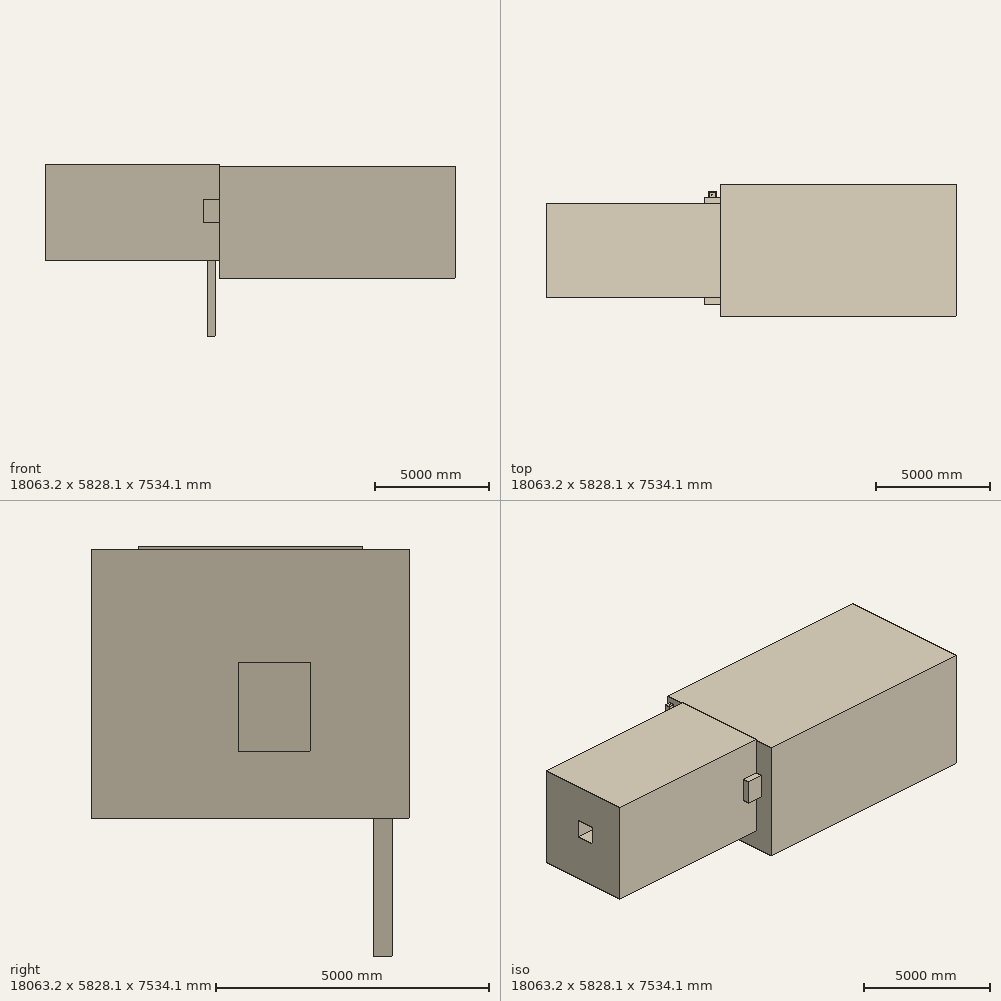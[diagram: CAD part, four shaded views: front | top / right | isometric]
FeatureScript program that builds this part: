
annotation { "Feature Type Name" : "Feature", "Feature Type Description" : "" }
export const myFeature = defineFeature(function(context is Context, id is Id, definition is map)
    precondition{}
    {
        {
            var Q0;
            Q0=qCreatedBy(makeId("Top.planeOp"),FACE);
            var sketch = newSketch(context, id + "F0", { "sketchPlane" : qUnion([Q0])});
            skLineSegment(sketch, "E0.bottom", {"start": v(-98.51, -97.6) * mm, "end": v(99.32, -97.6) * mm});
            skLineSegment(sketch, "E0.top", {"start": v(-98.51, 98.05) * mm, "end": v(99.32, 98.05) * mm});
            skLineSegment(sketch, "E0.left", {"start": v(-98.51, -97.6) * mm, "end": v(-98.51, 98.05) * mm});
            skLineSegment(sketch, "E0.right", {"start": v(99.32, -97.6) * mm, "end": v(99.32, 98.05) * mm});
            skSolve(sketch);
        }
        {
            var Q0;
            Q0 = qSketchRegion(id + "F0", true);
            extrude(context, id + "F1", {"entities" : qUnion([Q0]), "depth" : 1013.86 * mm, "offsetDistance" : 25.4 * mm});
        }
        {
            var Q0;
            Q0=makeQuery(id+"F1.opExtrude","CAP_FACE",FACE,{"disambiguationData":[OSD([sQuery(id+"F0.wireOp",EDGE,"E0.bottom"),sQuery(id+"F0.wireOp",EDGE,"E0.top"),sQuery(id+"F0.wireOp",EDGE,"E0.left"),sQuery(id+"F0.wireOp",EDGE,"E0.right")])],"isStart":false});
            var sketch = newSketch(context, id + "F2", { "sketchPlane" : qUnion([Q0])});
            skLineSegment(sketch, "E1.bottom", {"start": v(18.8, -27.3) * mm, "end": v(-23.04, -27.3) * mm});
            skLineSegment(sketch, "E1.top", {"start": v(18.8, 40.95) * mm, "end": v(-23.04, 40.95) * mm});
            skLineSegment(sketch, "E1.left", {"start": v(18.8, -27.3) * mm, "end": v(18.8, 40.95) * mm});
            skLineSegment(sketch, "E1.right", {"start": v(-23.04, -27.3) * mm, "end": v(-23.04, 40.95) * mm});
            skLineSegment(sketch, "E2.bottom", {"start": v(115.17, -114.66) * mm, "end": v(-117.42, -114.66) * mm});
            skLineSegment(sketch, "E2.top", {"start": v(115.17, 116.6) * mm, "end": v(-117.42, 116.6) * mm});
            skLineSegment(sketch, "E2.left", {"start": v(115.17, -114.66) * mm, "end": v(115.17, 116.6) * mm});
            skLineSegment(sketch, "E2.right", {"start": v(-117.42, -114.66) * mm, "end": v(-117.42, 116.6) * mm});
            skSolve(sketch);
        }
        {
            var Q0;
            Q0 = qSketchRegion(id + "F2", true);
            extrude(context, id + "F3", {"entities" : qUnion([Q0]), "operationType" : NewBodyOperationType.ADD, "depth" : 1544.75 * mm, "offsetDistance" : 25.4 * mm});
        }
        {
            var Q0;
            Q0=makeQuery(id+"F1.opExtrude","CAP_FACE",FACE,{"disambiguationData":[OSD([sQuery(id+"F0.wireOp",EDGE,"E0.bottom"),sQuery(id+"F0.wireOp",EDGE,"E0.top"),sQuery(id+"F0.wireOp",EDGE,"E0.left"),sQuery(id+"F0.wireOp",EDGE,"E0.right")])],"isStart":true});
            var sketch = newSketch(context, id + "F4", { "sketchPlane" : qUnion([Q0])});
            skCircle(sketch, "E3", {"center": v(0, 0) * mm, "radius": 62.15 * mm});
            skLineSegment(sketch, "E4.bottom", {"start": v(-166.8, -167.98) * mm, "end": v(171.05, -167.98) * mm});
            skLineSegment(sketch, "E4.top", {"start": v(-166.8, 166.77) * mm, "end": v(171.05, 166.77) * mm});
            skLineSegment(sketch, "E4.left", {"start": v(-166.8, -167.98) * mm, "end": v(-166.8, 166.77) * mm});
            skLineSegment(sketch, "E4.right", {"start": v(171.05, -167.98) * mm, "end": v(171.05, 166.77) * mm});
            skSolve(sketch);
        }
        {
            var Q0;
            Q0 = qSketchRegion(id + "F4", true);
            extrude(context, id + "F5", {"entities" : qUnion([Q0]), "operationType" : NewBodyOperationType.ADD, "depth" : 4867.7 * mm, "offsetDistance" : 25.4 * mm});
        }
        {
            var Q0;
            Q0=makeQuery(id+"F1.opExtrude","SWEPT_FACE",FACE,{"disambiguationData":[OSD([sQuery(id+"F0.wireOp",EDGE,"E0.bottom")])]});
            var sketch = newSketch(context, id + "F6", { "sketchPlane" : qUnion([Q0])});
            skLineSegment(sketch, "E5.bottom", {"start": v(362.37, 148.89) * mm, "end": v(-363.95, 148.89) * mm});
            skLineSegment(sketch, "E5.top", {"start": v(362.37, 519.84) * mm, "end": v(-363.95, 519.84) * mm});
            skLineSegment(sketch, "E5.left", {"start": v(362.37, 148.89) * mm, "end": v(362.37, 519.84) * mm});
            skLineSegment(sketch, "E5.right", {"start": v(-363.95, 148.89) * mm, "end": v(-363.95, 519.84) * mm});
            skLineSegment(sketch, "E6.bottom", {"start": v(362.37, 519.84) * mm, "end": v(42.88, 519.84) * mm});
            skLineSegment(sketch, "E6.top", {"start": v(362.37, 769.88) * mm, "end": v(42.88, 769.88) * mm});
            skLineSegment(sketch, "E6.left", {"start": v(362.37, 519.84) * mm, "end": v(362.37, 769.88) * mm});
            skLineSegment(sketch, "E6.right", {"start": v(42.88, 519.84) * mm, "end": v(42.88, 769.88) * mm});
            skLineSegment(sketch, "E7.bottom", {"start": v(99.32, 769.88) * mm, "end": v(359.68, 769.88) * mm});
            skLineSegment(sketch, "E7.top", {"start": v(99.32, 874.98) * mm, "end": v(359.68, 874.98) * mm});
            skLineSegment(sketch, "E7.left", {"start": v(99.32, 769.88) * mm, "end": v(99.32, 874.98) * mm});
            skLineSegment(sketch, "E7.right", {"start": v(359.68, 769.88) * mm, "end": v(359.68, 874.98) * mm});
            skSolve(sketch);
        }
        {
            var Q0;
            {var subQ0=sQuery(id+"F6.wireOp",EDGE,"E6.right");Q0=makeQuery(id+"F6.imprint","IMPRINT",FACE,{"disambiguationData":[TD([[makeQuery(id+"F6.imprint","IMPRINT",EDGE,{"derivedFrom":subQ0}),1.0]])]});}
            var sketch = newSketch(context, id + "F7", { "sketchPlane" : qUnion([Q0])});
            skLineSegment(sketch, "E8.bottom", {"start": v(366.89, 151.33) * mm, "end": v(-364.8, 151.33) * mm});
            skLineSegment(sketch, "E8.top", {"start": v(366.89, 1125.47) * mm, "end": v(-364.8, 1125.47) * mm});
            skLineSegment(sketch, "E8.left", {"start": v(366.89, 151.33) * mm, "end": v(366.89, 1125.47) * mm});
            skLineSegment(sketch, "E8.right", {"start": v(-364.8, 151.33) * mm, "end": v(-364.8, 1125.47) * mm});
            skSolve(sketch);
        }
        {
            var Q0;
            Q0 = qSketchRegion(id + "F7", true);
            extrude(context, id + "F8", {"entities" : qUnion([Q0]), "operationType" : NewBodyOperationType.ADD, "depth" : 4697.9 * mm, "offsetDistance" : 25.4 * mm});
        }
        {
            var Q0;
            Q0=makeQuery(id+"F8.opExtrude","SWEPT_FACE",FACE,{"disambiguationData":[OSD([sQuery(id+"F7.wireOp",EDGE,"E8.left")])]});
            var sketch = newSketch(context, id + "F9", { "sketchPlane" : qUnion([Q0])});
            skLineSegment(sketch, "E9.bottom", {"start": v(-4499.5, 2666.45) * mm, "end": v(-377.14, 2666.45) * mm});
            skLineSegment(sketch, "E9.top", {"start": v(-4499.5, -1543.2) * mm, "end": v(-377.14, -1543.2) * mm});
            skLineSegment(sketch, "E9.left", {"start": v(-4499.5, 2666.45) * mm, "end": v(-4499.5, -1543.2) * mm});
            skLineSegment(sketch, "E9.right", {"start": v(-377.14, 2666.45) * mm, "end": v(-377.14, -1543.2) * mm});
            skLineSegment(sketch, "E10.bottom", {"start": v(-2193.41, 373.98) * mm, "end": v(-2941.75, 373.98) * mm});
            skLineSegment(sketch, "E10.top", {"start": v(-2193.41, 1125.47) * mm, "end": v(-2941.75, 1125.47) * mm});
            skLineSegment(sketch, "E10.left", {"start": v(-2193.41, 373.98) * mm, "end": v(-2193.41, 1125.47) * mm});
            skLineSegment(sketch, "E10.right", {"start": v(-2941.75, 373.98) * mm, "end": v(-2941.75, 1125.47) * mm});
            skSolve(sketch);
        }
        {
            var Q0;
            Q0 = qSketchRegion(id + "F9", true);
            extrude(context, id + "F10", {"entities" : qUnion([Q0]), "operationType" : NewBodyOperationType.ADD, "oppositeDirection" : true, "depth" : 7675.83 * mm, "offsetDistance" : 25.4 * mm});
        }
        {
            var Q0;
            Q0=makeQuery(id+"F10.boolean.opBoolean","MERGE",FACE,{"derivedFrom":[makeQuery(id+"F8.opExtrude","SWEPT_FACE",FACE,{"disambiguationData":[OSD([sQuery(id+"F7.wireOp",EDGE,"E8.left")])]}),makeQuery(id+"F10.opExtrude","CAP_FACE",FACE,{"disambiguationData":[OSD([sQuery(id+"F9.wireOp",EDGE,"E9.bottom"),sQuery(id+"F9.wireOp",EDGE,"E9.top"),sQuery(id+"F9.wireOp",EDGE,"E9.left"),sQuery(id+"F9.wireOp",EDGE,"E9.right"),sQuery(id+"F9.wireOp",EDGE,"E10.bottom"),sQuery(id+"F9.wireOp",EDGE,"E10.top"),sQuery(id+"F9.wireOp",EDGE,"E10.left"),sQuery(id+"F9.wireOp",EDGE,"E10.right")])],"isStart":true})]});
            var sketch = newSketch(context, id + "F11", { "sketchPlane" : qUnion([Q0])});
            skLineSegment(sketch, "E11.bottom", {"start": v(-5349.96, -2334.38) * mm, "end": v(478.18, -2334.38) * mm});
            skLineSegment(sketch, "E11.top", {"start": v(-5349.96, 2617.81) * mm, "end": v(478.18, 2617.81) * mm});
            skLineSegment(sketch, "E11.left", {"start": v(-5349.96, -2334.38) * mm, "end": v(-5349.96, 2617.81) * mm});
            skLineSegment(sketch, "E11.right", {"start": v(478.18, -2334.38) * mm, "end": v(478.18, 2617.81) * mm});
            skLineSegment(sketch, "E12.bottom", {"start": v(-2661.49, 537.44) * mm, "end": v(-1327.12, 537.44) * mm});
            skLineSegment(sketch, "E12.top", {"start": v(-2661.49, -1100.5) * mm, "end": v(-1327.12, -1100.5) * mm});
            skLineSegment(sketch, "E12.left", {"start": v(-2661.49, 537.44) * mm, "end": v(-2661.49, -1100.5) * mm});
            skLineSegment(sketch, "E12.right", {"start": v(-1327.12, 537.44) * mm, "end": v(-1327.12, -1100.5) * mm});
            skSolve(sketch);
        }
        {
            var Q0;
            Q0 = qSketchRegion(id + "F11", true);
            extrude(context, id + "F12", {"entities" : qUnion([Q0]), "operationType" : NewBodyOperationType.ADD, "depth" : 10387.4 * mm, "offsetDistance" : 25.4 * mm});
        }
    });
